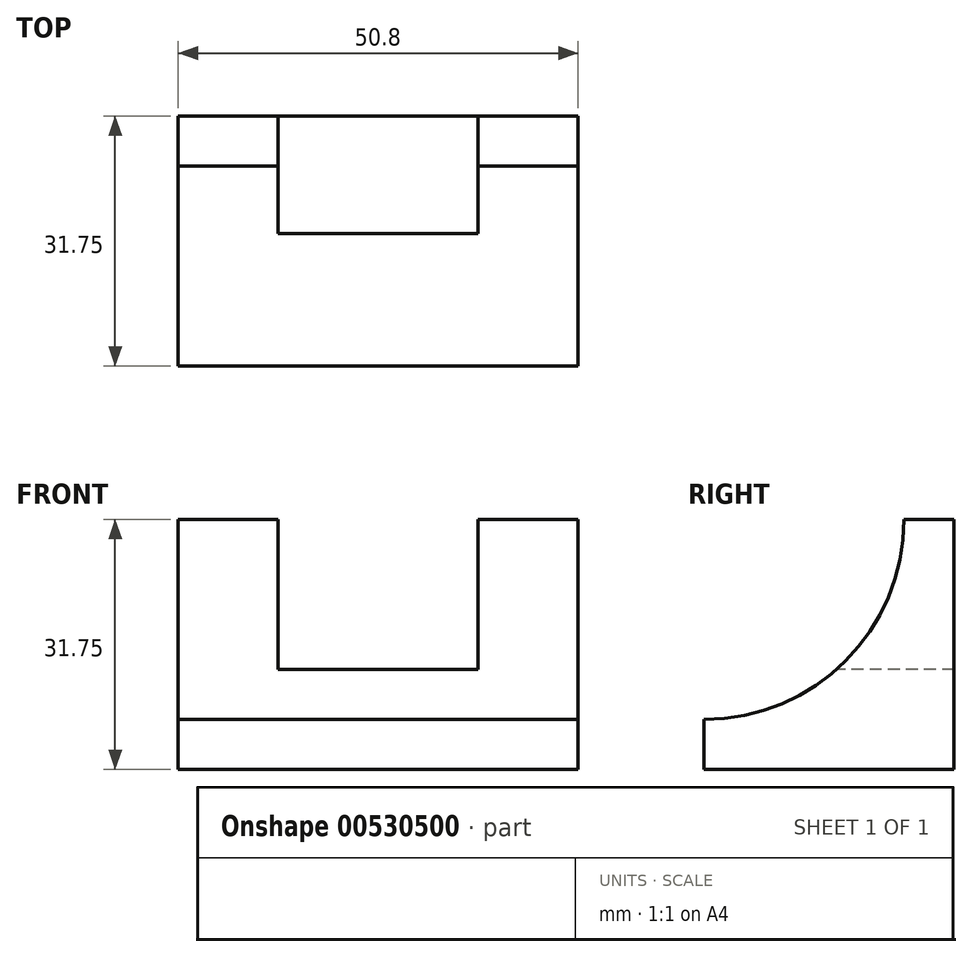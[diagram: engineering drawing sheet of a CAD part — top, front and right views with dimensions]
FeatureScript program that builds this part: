
annotation { "Feature Type Name" : "Feature", "Feature Type Description" : "" }
export const myFeature = defineFeature(function(context is Context, id is Id, definition is map)
    precondition{}
    {
        {
            var Q0;
            Q0=qCreatedBy(makeId("Front.planeOp"),FACE);
            var sketch = newSketch(context, id + "F0", { "sketchPlane" : qUnion([Q0])});
            skLineSegment(sketch, "E0", {"start": v(0, 0) * mm, "end": v(50.8, 0) * mm});
            skLineSegment(sketch, "E1", {"start": v(50.8, 0) * mm, "end": v(50.8, 31.75) * mm});
            skLineSegment(sketch, "E2", {"start": v(50.8, 31.75) * mm, "end": v(0, 31.75) * mm});
            skLineSegment(sketch, "E3", {"start": v(0, 31.75) * mm, "end": v(0, 0) * mm});
            skSolve(sketch);
        }
        {
            var Q0;
            Q0 = qSketchRegion(id + "F0", true);
            extrude(context, id + "F1", {"entities" : qUnion([Q0]), "depth" : 31.75 * mm, "offsetDistance" : 25.4 * mm});
        }
        {
            var Q0;
            Q0=makeQuery(id+"F1.opExtrude","CAP_FACE",FACE,{"disambiguationData":[OSD([sQuery(id+"F0.wireOp",EDGE,"E0"),sQuery(id+"F0.wireOp",EDGE,"E1"),sQuery(id+"F0.wireOp",EDGE,"E2"),sQuery(id+"F0.wireOp",EDGE,"E3")])],"isStart":false});
            var sketch = newSketch(context, id + "F2", { "sketchPlane" : qUnion([Q0])});
            skLineSegment(sketch, "E4.bottom", {"start": v(12.7, 31.75) * mm, "end": v(38.1, 31.75) * mm});
            skLineSegment(sketch, "E4.top", {"start": v(12.7, 12.7) * mm, "end": v(38.1, 12.7) * mm});
            skLineSegment(sketch, "E4.left", {"start": v(12.7, 31.75) * mm, "end": v(12.7, 12.7) * mm});
            skLineSegment(sketch, "E4.right", {"start": v(38.1, 31.75) * mm, "end": v(38.1, 12.7) * mm});
            skSolve(sketch);
        }
        {
            var Q0;
            Q0=makeQuery(id+"F2.imprint","IMPRINT",FACE,{"disambiguationData":[TD([[makeQuery(id+"F2.imprint","IMPRINT",EDGE,{"derivedFrom":sQuery(id+"F2.wireOp",EDGE,"E4.bottom")}),1.0]])]});
            extrude(context, id + "F3", {"entities" : qUnion([Q0]), "operationType" : NewBodyOperationType.REMOVE, "endBound" : BoundingType.THROUGH_ALL, "oppositeDirection" : true, "depth" : 25.4 * mm, "offsetDistance" : 25.4 * mm});
        }
        {
            var Q0;
            Q0=makeQuery(id+"F1.opExtrude","SWEPT_FACE",FACE,{"disambiguationData":[OSD([sQuery(id+"F0.wireOp",EDGE,"E1")])]});
            var sketch = newSketch(context, id + "F4", { "sketchPlane" : qUnion([Q0])});
            skCircle(sketch, "E5", {"center": v(-31.75, 31.75) * mm, "radius": 25.4 * mm});
            skSolve(sketch);
        }
        {
            var Q0;
            Q0 = qSketchRegion(id + "F4", true);
            extrude(context, id + "F5", {"entities" : qUnion([Q0]), "operationType" : NewBodyOperationType.REMOVE, "endBound" : BoundingType.THROUGH_ALL, "oppositeDirection" : true, "depth" : 25.4 * mm, "offsetDistance" : 25.4 * mm});
        }
    });
